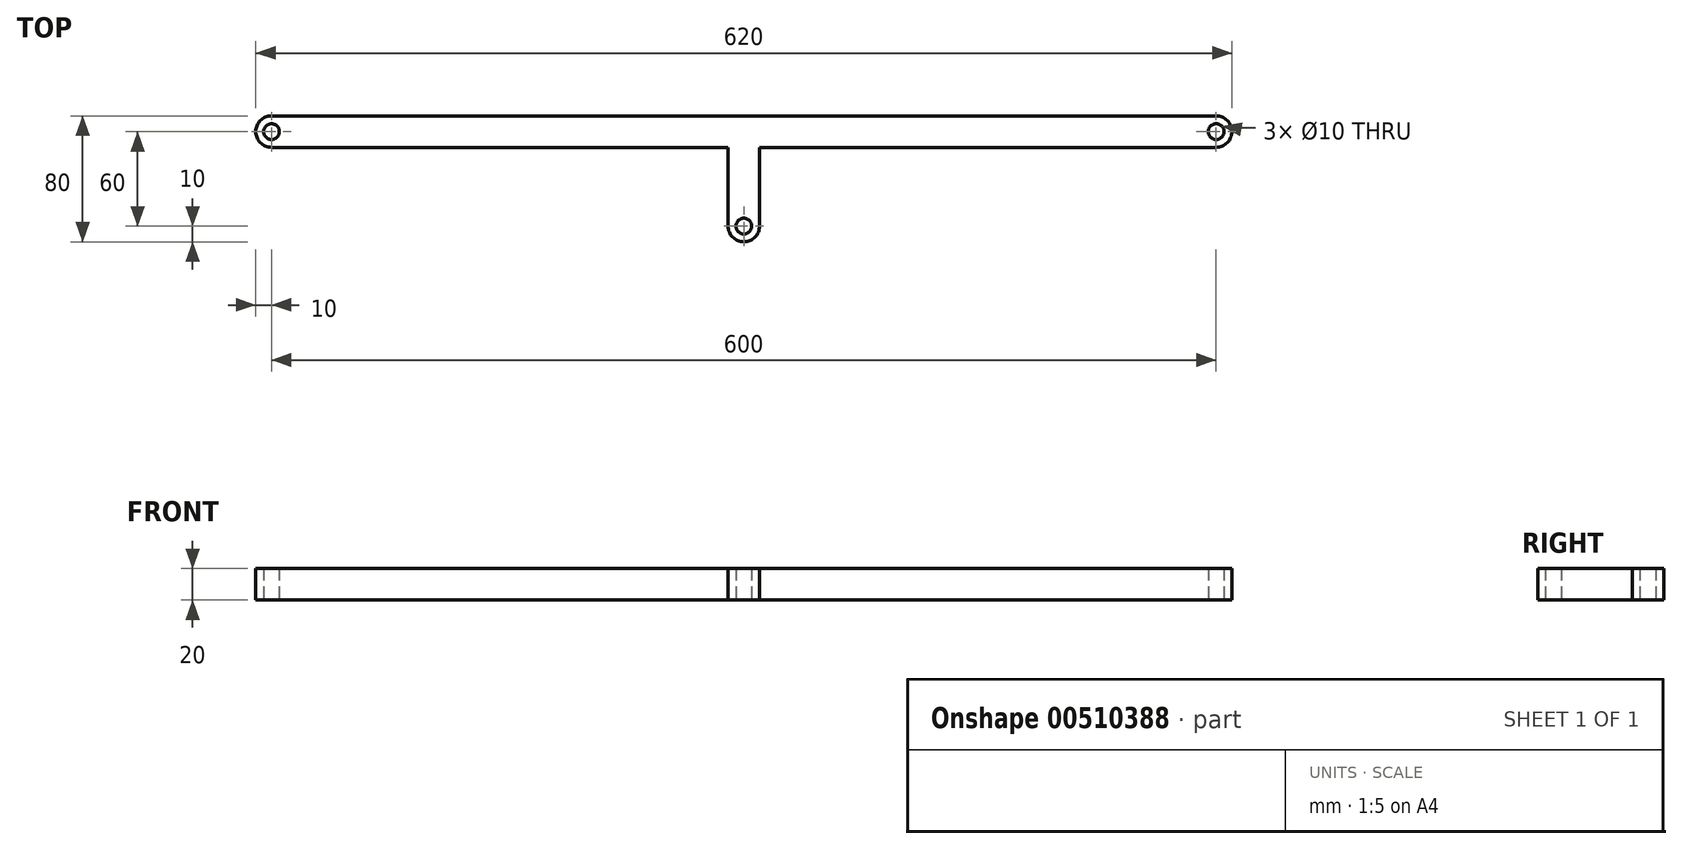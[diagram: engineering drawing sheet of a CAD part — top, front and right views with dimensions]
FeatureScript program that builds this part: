
annotation { "Feature Type Name" : "Feature", "Feature Type Description" : "" }
export const myFeature = defineFeature(function(context is Context, id is Id, definition is map)
    precondition{}
    {
        {
            var Q0;
            Q0=qCreatedBy(makeId("Top.planeOp"),FACE);
            var sketch = newSketch(context, id + "F0", { "sketchPlane" : qUnion([Q0])});
            skLineSegment(sketch, "E0.bottom", {"start": v(0, 0) * mm, "end": v(290, 0) * mm});
            skLineSegment(sketch, "E0.top", {"start": v(0, 20) * mm, "end": v(600, 20) * mm});
            skArc(sketch, "E1", {"start": v(600, 0) * mm, "mid": v(610, 10) * mm, "end": v(600, 20) * mm});
            skCircle(sketch, "E2", {"center": v(600, 10) * mm, "radius": 5 * mm});
            skArc(sketch, "E3", {"start": v(0, 20) * mm, "mid": v(-10, 10) * mm, "end": v(0, 0) * mm});
            skCircle(sketch, "E4", {"center": v(0, 10) * mm, "radius": 5 * mm});
            skLineSegment(sketch, "E5", {"start": v(300, 0) * mm, "end": v(300, -86.35) * mm, "construction": true});
            skLineSegment(sketch, "E6", {"start": v(310, 0) * mm, "end": v(310, -50) * mm});
            skLineSegment(sketch, "E7.MirrorCS", {"start": v(290, 0) * mm, "end": v(290, -50) * mm});
            skArc(sketch, "E8", {"start": v(290, -50) * mm, "mid": v(300, -60) * mm, "end": v(310, -50) * mm});
            skCircle(sketch, "E9", {"center": v(300, -50) * mm, "radius": 5 * mm});
            skLineSegment(sketch, "E10.trimOffspring", {"start": v(310, 0) * mm, "end": v(600, 0) * mm});
            skSolve(sketch);
        }
        {
            var Q0;
            Q0=makeQuery(id+"F0.imprint","IMPRINT",FACE,{"disambiguationData":[TD([[makeQuery(id+"F0.imprint","IMPRINT",EDGE,{"derivedFrom":sQuery(id+"F0.wireOp",EDGE,"E0.bottom")}),1.0]])]});
            extrude(context, id + "F1", {"entities" : qUnion([Q0]), "endBound" : BoundingType.SYMMETRIC, "depth" : 20 * mm});
        }
    });
